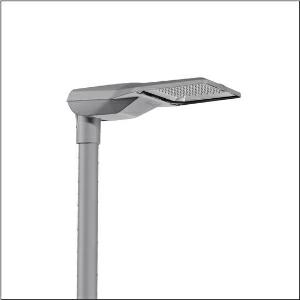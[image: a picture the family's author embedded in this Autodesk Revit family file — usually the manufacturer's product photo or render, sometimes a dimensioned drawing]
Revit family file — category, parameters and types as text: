
# Revit family: streetlight_sl_21_iq_midi___pl52_5xe3h31g08mb_961f
name_source: partatom
category: Lighting Fixtures
units: mm (PartAtom-declared; Revit-internal decimal feet)

## family parameters
Cut with Voids When Loaded = No
Host = Face
Light Source = No
Part Type = Normal
Room Calculation Point = No
Round Connector Dimension = Use Diameter
Shared = No

## types (1)
- --- (1 x LED, 19170 lm, 146.7 W, 3000K)
    Apparent Load = 147 VA
    CIE Flux Codes = 27 59 98 100 100
    Color Rendering = 70
    Color Temperature = 3000K
    Default Elevation = 1800 mm
    Description = Streetlight SL 21 iQ midi, mast luminaire, primary light control with lens, of PMMA, primary optical cover: cover, of toughened safety glass, transparent, light distribution: PL52, light emission: direct distribution, primary light characteristic: asymmetric, installation type: post-top, side-entry, LED, High Power LED, rated luminous flux: 19.170lm, luminous efficacy: 131lm/W, light colour: 730, colour temperature: 3000K, control: Street-Remote, Auto-Match, Temp-Guard, Lumen-Switch, Night-Set, Smart-Wire, Light-Fading, Desk-Remote (wireless, voltage-free reading and setting of iQ features in the workshop via application-optimized NFC function/RFID function), optimised constant luminous flux control (CLO 2.0), presetting dimming linear, mains connection: 230..240V, AC, 50/60Hz, start of lifetime: 147W, end of service life: 161W, reduction: 62W, luminaire housing, of diecast aluminium, powder-coated, Siteco® metallic grey (DB 702S), corrosivity category C5 mid according to DIN EN ISO 12944, please order mast flange separately, inclination adjustable: 0°, 5°, 10°, 15°, sealing non-destructively replaceable, multi-level sealing system, length: 644mm, width: 335mm, height: 110mm, mast flange for spigot size: 42mm (side-entry): 5XC10008XM4, 60/48mm (side-entry/post-top): 5XC10108XM2, 76/60mm (side-entry/post-top): 5XC10108XM1, protection rating (complete): IP66, insulation class (complete): insulation class II (safety insulation), certification: CE, ENEC, ENEC+, VDE, impact resistance: IK09, permissible operating ambient temperature for outdoor applications: -40..+50°C, standard-compliant lighting for roads and squares, packaging unit: 1 piece

Light Distribution: PL52
    Height = 111 mm
    Lamp = 1 x LED
    Lamp Light Flux = 19170 lm
    Lamp Power = 146.7 W
    Lamp count = 1
    Length = 644 mm
    Luminous efficacy = 131 lm/W
    Manufacturer = Siteco
    ModVariant = No
    Model = 5XE3H31G08MB
    Number of Poles = 1
    OnlyDefault = Yes
    Power Factor = 1
    Product Name = Streetlight SL 21 iQ midi | PL52
    Product group = mast luminaire | pylon top
    ProductGroupID = 6100
    Protection Class = Protection class II
    Protection Degree = IP 66
    RLX_Detail_Level = 1
    RLX_Emergency_Light_Flux = 0 lm
    RLX_Emergency_Type = 0
    RLX_Emergency_Type_DB = No
    RlxData = <blob elided: 100269 chars, md5=6f430d22>
    Socket = socket
    Standby Power = 0 W
    System Light Flux = 19169 lm
    System Power = 147 W
    Type Comments = factory setting: luminous flux: 100 % | dim-lin: 254 | 753 mA
    Type Image = l_1004298.jpg
    URL = http://relux.com
    VarID = @adj_143255
    Voltage = 0 V
    Weight = 0.00 kg
    Width = 336 mm

## geometry (parser evidence)
native form markers: Blend x4, Sweep x10
no freeform markers — native parametric forms only
